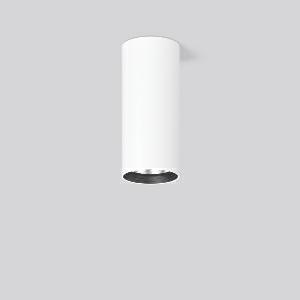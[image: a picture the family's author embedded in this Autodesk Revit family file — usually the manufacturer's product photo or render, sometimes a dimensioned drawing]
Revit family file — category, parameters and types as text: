
# Revit family: heledon_mini_a_931200_002_1_76_7923
name_source: partatom
category: Lighting Fixtures
units: mm (PartAtom-declared; Revit-internal decimal feet)

## family parameters
Cut with Voids When Loaded = No
Host = Face
Light Source = No
Part Type = Normal
Room Calculation Point = No
Round Connector Dimension = Use Diameter
Shared = No

## types (1)
- HELEDON mini A (1 x LED Modul 940, 2700 lm, 4000)
    Apparent Load = 20 VA
    Approval mark = CE
    CIE Flux Codes = 100 100 100 100 100
    Color Rendering = 92
    Color Temperature = 4000
    Default Elevation = 1800 mm
    Description = Series: HELEDON mini
Cylindrical surface-mounted downlight. Housing: die-cast aluminium, powder-coated. Internal ceiling frame polycarbonate with bayonet mounting. Black plastic ring and recessed LED to prevent glare from the side. Optical assembly with reflector made of MIRO-Silver with 98% total light reflection for outstanding efficiency - can be changed without tools. Best colour rendering index Ra>90. Suitable for Ceiling mounting. Easy installation with a separate ceiling frame with bayonet mounting and plug connection. Driver integrated. Connected via plug-in connector. High quality converter without flickering and stroboscopic effect. The following accessories can be mounted without use of tools: interchangeable lenses, decorative glasses, honeycomb louvre, clear and frosted diffusers, white interchangeable plastic ring. 
Colour: traffic white, matt (RAL 9016)
Diameter: 87 mm
Height: 197 mm
Lamp: LED
Socket: without socket
Colour temperature: 4000K
Colour rendering index (CRI): 92
System power: 20 W
Rated luminous flux: 2700 lm
Luminous efficiency: 135 lm/W
Control gear: Converter, dimmable, DALI
Protection class: I
Type of protection: IP 20
    Height = 197 mm
    Lamp = 1 x LED Modul 940
    Lamp Light Flux = 2700 lm
    Lamp count = 1
    Length = 87 mm
    Lifetime = 50000 h
    Luminous efficacy = 135 lm/W
    Manufacturer = RZB
    ModVariant = No
    Model = 931200.002.1.76
    Mounting Place = Ceiling
    Mounting Type = Surface mounted
    Number of Poles = 1
    OnlyDefault = Yes
    Power Factor = 1
    Product Name = HELEDON mini A
    Product group = Surface mounted downlights
    ProductGroupID = 302
    Protection Class = Protection class I
    Protection Degree = IP 20
    RLX_Detail_Level = 1
    RLX_Emergency_Light_Flux = 0 lm
    RLX_Emergency_Type = 0
    RLX_Emergency_Type_DB = No
    RlxData = <blob elided: 104025 chars, md5=25042d6e>
    Socket = socket
    Standby Power = 0 W
    System Light Flux = 2700 lm
    System Power = 20 W
    Type Comments = Product without accessories
    Type Image = 931188.002.jpg
    URL = http://relux.com
    VarID = ---
    Voltage = 230 V
    Voltage Range = 220-240 V
    Weight = 0.00 kg
    Width = 0 mm  [stored 0 ft]

note: [stored X ft] marks values corroborated as IEEE doubles in the binary element streams (Revit-internal decimal feet)

## geometry (parser evidence)
native form markers: Blend x4, Sweep x10
no freeform markers — native parametric forms only
